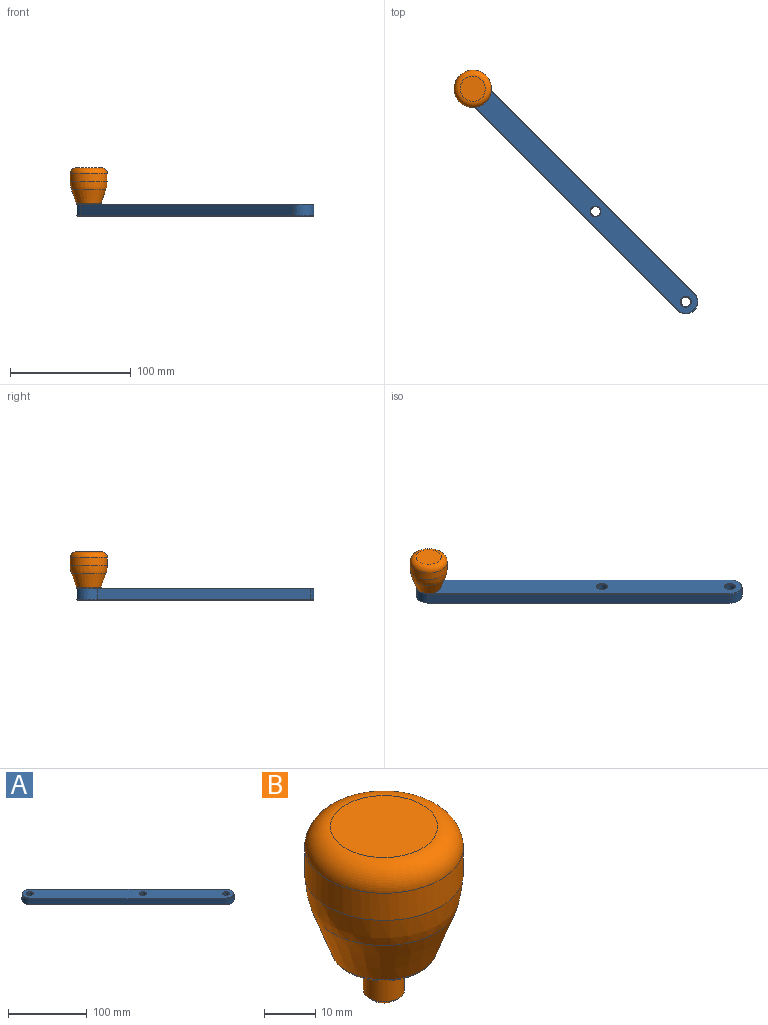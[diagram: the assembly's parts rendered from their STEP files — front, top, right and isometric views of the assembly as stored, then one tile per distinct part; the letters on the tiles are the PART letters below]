
ASSEMBLY  parts=2 mates=1
PART A: 23 faces, bbox 196.8x196.8x10 mm
  f0: plane 176.78x176.78mm, normal (0.71,0.71,0), area 2250mm2, adj f1,f6,f12,f19
  f1: cylinder r=10mm len=17.07mm, axis (0,0,-1), area 282.7mm2, adj f0,f2,f14,f21
  f2: plane 176.78x176.78mm, normal (-0.71,-0.71,0), area 2250mm2, adj f1,f6,f13,f20
  f3: cylinder r=4mm len=9mm, axis (0,0,-1), area 226.2mm2, adj f15,f22
  f4: cylinder r=4mm len=9mm, axis (0,0,-1), area 226.2mm2, adj f10,f17
  f5: cylinder r=4mm len=9mm, axis (0,0,-1), area 226.2mm2, adj f9,f16
  f6: cylinder r=10mm len=17.07mm, axis (0,0,-1), area 282.7mm2, adj f0,f2,f11,f18
  f7: plane 195.78x195.78mm, normal (0,0,1), area 4842.7mm2, adj f16,f17,f18,f19,f20,f21,f22
  f8: plane 195.78x195.78mm, normal (0,0,-1), area 4842.7mm2, adj f9,f10,f11,f12,f13,f14,f15
  f9: cone r=4.5mm half-angle=45deg, axis (0,0,-1), area 18.9mm2, adj f5,f8
  f10: cone r=4.5mm half-angle=45deg, axis (0,0,-1), area 18.9mm2, adj f4,f8
  f11: cone r=10mm half-angle=45deg, axis (0,0,1), area 21.7mm2, adj f6,f8,f12,f13
  f12: plane 177.13x177.13mm, normal (0.5,0.5,-0.71), area 176.8mm2, adj f0,f8,f11,f14
  f13: plane 177.13x177.13mm, normal (-0.5,-0.5,-0.71), area 176.8mm2, adj f2,f8,f11,f14
  f14: cone r=10mm half-angle=45deg, axis (0,0,1), area 21.7mm2, adj f1,f8,f12,f13
  f15: cone r=4.5mm half-angle=45deg, axis (0,0,-1), area 18.9mm2, adj f3,f8
  f16: cone r=4mm half-angle=45deg, axis (0,0,1), area 18.9mm2, adj f5,f7
  f17: cone r=4mm half-angle=45deg, axis (0,0,1), area 18.9mm2, adj f4,f7
  f18: cone r=9.5mm half-angle=45deg, axis (0,0,-1), area 21.7mm2, adj f6,f7,f19,f20
  f19: plane 177.13x177.13mm, normal (0.5,0.5,0.71), area 176.8mm2, adj f0,f7,f18,f21
  f20: plane 177.13x177.13mm, normal (-0.5,-0.5,0.71), area 176.8mm2, adj f2,f7,f18,f21
  f21: cone r=9.5mm half-angle=45deg, axis (0,0,-1), area 21.7mm2, adj f1,f7,f19,f20
  f22: cone r=4mm half-angle=45deg, axis (0,0,1), area 18.9mm2, adj f3,f7
PART B: 10 faces, bbox 33.5x33.5x40 mm
  f0: plane 6x6mm, normal (0,0,-1), area 28.3mm2, adj f9
  f1: cylinder r=4mm len=9mm, axis (0,0,1), area 226.2mm2, adj f3,f9
  f2: cone r=10mm half-angle=20deg, axis (0,0,1), area 903mm2, adj f6,f8
  f3: plane 18.6x18.6mm, normal (0,0,-1), area 221.4mm2, adj f1,f8
  f4: cylinder r=15.46mm len=30.92mm, axis (0,0,-1), area 628.8mm2, adj f6,f7
  f5: plane 20.92x20.92mm, normal (0,0,1), area 343.7mm2, adj f7
  f6: revolved ~30.92x30.92mm, area 1320.8mm2, adj f2,f4
  f7: torus R=10.46mm, axis (0,0,1), area 673.2mm2, adj f4,f5
  f8: torus R=9.3mm, axis (0,0,1), area 75.5mm2, adj f2,f3
  f9: cone r=3mm half-angle=45deg, axis (0,0,1), area 31.1mm2, adj f0,f1
PLACE A at identity fixed
PLACE B at identity
MATE revolute A.f1 <-> B.f1  axis (0,0,1) through (-176.78,101.78,45)mm
